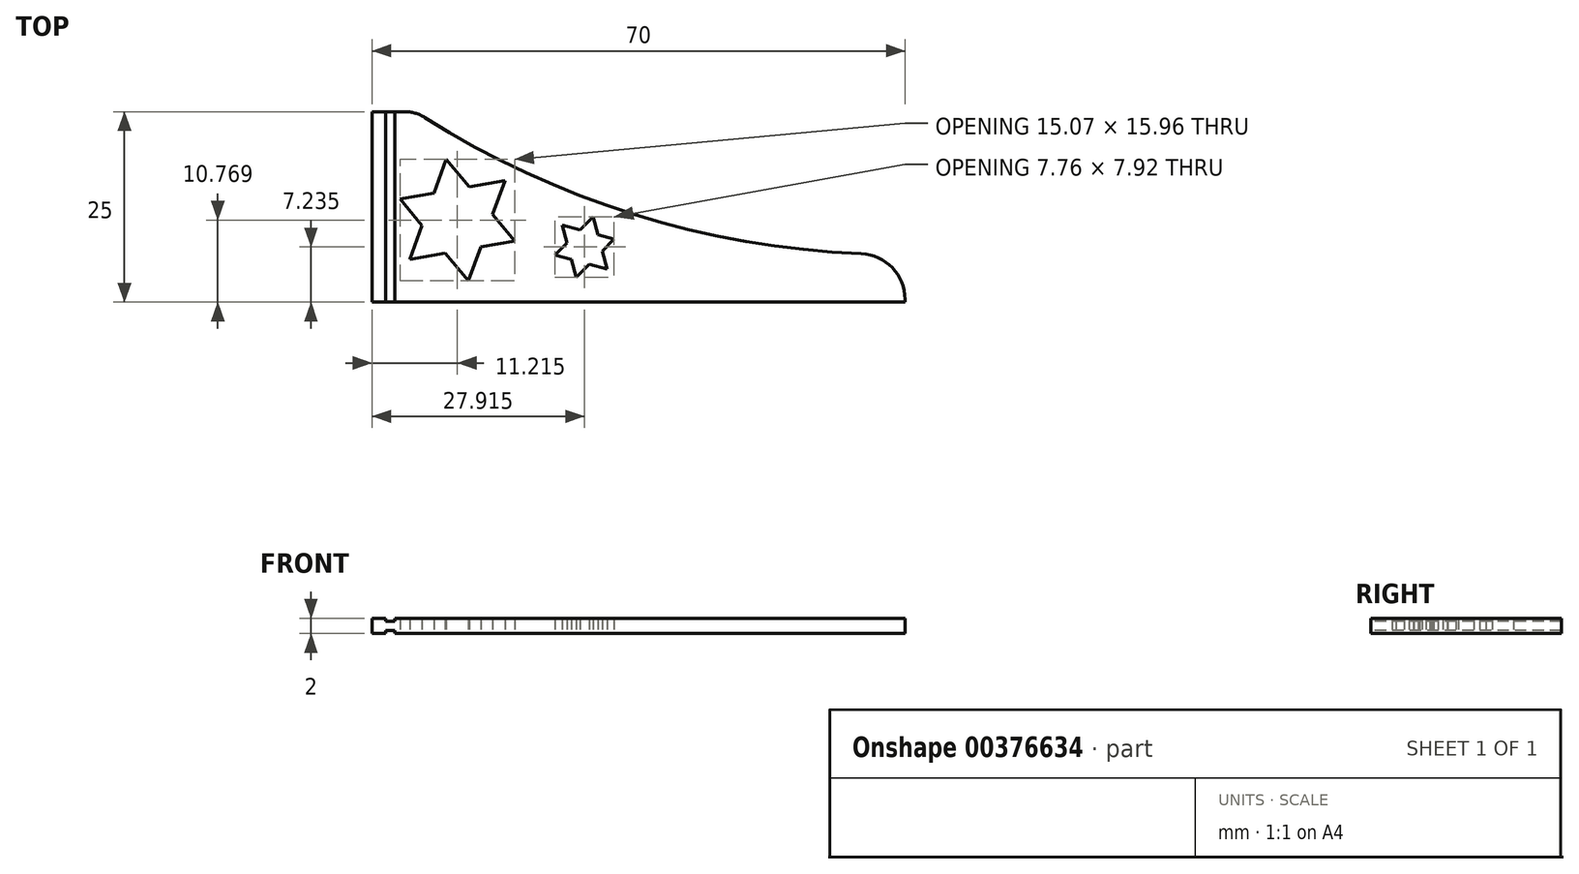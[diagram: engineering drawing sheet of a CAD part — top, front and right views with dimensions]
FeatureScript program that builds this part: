
annotation { "Feature Type Name" : "Feature", "Feature Type Description" : "" }
export const myFeature = defineFeature(function(context is Context, id is Id, definition is map)
    precondition{}
    {
        {
            var Q0;
            Q0=qCreatedBy(makeId("Top.planeOp"),FACE);
            var sketch = newSketch(context, id + "F0", { "sketchPlane" : qUnion([Q0])});
            skLineSegment(sketch, "E0.bottom", {"start": v(0, 0) * mm, "end": v(70, 0) * mm});
            skLineSegment(sketch, "E0.top", {"start": v(0, 25) * mm, "end": v(4.27, 25) * mm});
            skLineSegment(sketch, "E0.left", {"start": v(0, 0) * mm, "end": v(0, 25) * mm});
            skLineSegment(sketch, "E0.right", {"start": v(70, 0) * mm, "end": v(70, 0.35) * mm});
            skArc(sketch, "E1", {"start": v(6.95, 24.22) * mm, "mid": v(34.42, 11.5) * mm, "end": v(64.24, 6.35) * mm});
            skArc(sketch, "E2.filletArc", {"start": v(70, 0.35) * mm, "mid": v(68.33, 4.5) * mm, "end": v(64.24, 6.35) * mm});
            skArc(sketch, "E3.filletArc", {"start": v(6.95, 24.22) * mm, "mid": v(5.66, 24.8) * mm, "end": v(4.27, 25) * mm});
            skLineSegment(sketch, "E4", {"start": v(17.47, 15.94) * mm, "end": v(12.8, 15.12) * mm});
            skLineSegment(sketch, "E5", {"start": v(3.68, 13.51) * mm, "end": v(6.58, 10.05) * mm});
            skLineSegment(sketch, "E6", {"start": v(17.47, 15.94) * mm, "end": v(15.85, 11.49) * mm});
            skLineSegment(sketch, "E7", {"start": v(9.75, 18.75) * mm, "end": v(8.13, 14.3) * mm});
            skLineSegment(sketch, "E8", {"start": v(4.96, 5.6) * mm, "end": v(9.63, 6.42) * mm});
            skLineSegment(sketch, "E9", {"start": v(18.75, 8.03) * mm, "end": v(15.85, 11.49) * mm});
            skLineSegment(sketch, "E10.trimOffspring", {"start": v(8.13, 14.3) * mm, "end": v(3.68, 13.51) * mm});
            skLineSegment(sketch, "E11.trimOffspring", {"start": v(12.8, 15.12) * mm, "end": v(9.75, 18.75) * mm});
            skLineSegment(sketch, "E12.trimOffspring", {"start": v(14.3, 7.24) * mm, "end": v(12.68, 2.79) * mm});
            skLineSegment(sketch, "E13.trimOffspring", {"start": v(14.3, 7.24) * mm, "end": v(18.75, 8.03) * mm});
            skLineSegment(sketch, "E14.trimOffspring", {"start": v(9.63, 6.42) * mm, "end": v(12.68, 2.79) * mm});
            skLineSegment(sketch, "E15.trimOffspring", {"start": v(6.58, 10.05) * mm, "end": v(4.96, 5.6) * mm});
            skLineSegment(sketch, "E16.0", {"start": v(29.03, 11.2) * mm, "end": v(27.31, 9.48) * mm});
            skLineSegment(sketch, "E16.1", {"start": v(28.52, 5) * mm, "end": v(30.86, 4.36) * mm});
            skLineSegment(sketch, "E16.2", {"start": v(30.23, 6.71) * mm, "end": v(30.86, 4.36) * mm});
            skLineSegment(sketch, "E16.3", {"start": v(30.23, 6.71) * mm, "end": v(31.8, 8.28) * mm});
            skLineSegment(sketch, "E16.4", {"start": v(31.8, 8.28) * mm, "end": v(29.66, 8.85) * mm});
            skLineSegment(sketch, "E16.5", {"start": v(26.8, 3.27) * mm, "end": v(28.52, 5) * mm});
            skLineSegment(sketch, "E16.6", {"start": v(29.03, 11.2) * mm, "end": v(29.66, 8.85) * mm});
            skLineSegment(sketch, "E16.7", {"start": v(26.17, 5.62) * mm, "end": v(26.8, 3.27) * mm});
            skLineSegment(sketch, "E16.8", {"start": v(24.03, 6.2) * mm, "end": v(26.17, 5.62) * mm});
            skLineSegment(sketch, "E16.9", {"start": v(25.6, 7.76) * mm, "end": v(24.03, 6.2) * mm});
            skLineSegment(sketch, "E16.10", {"start": v(24.97, 10.1) * mm, "end": v(25.6, 7.76) * mm});
            skLineSegment(sketch, "E16.11", {"start": v(27.31, 9.48) * mm, "end": v(24.97, 10.1) * mm});
            skSolve(sketch);
        }
        {
            var Q0;
            Q0=makeQuery(id+"F0.imprint","IMPRINT",FACE,{"disambiguationData":[TD([[makeQuery(id+"F0.imprint","IMPRINT",EDGE,{"derivedFrom":sQuery(id+"F0.wireOp",EDGE,"E0.bottom")}),1.0]])]});
            extrude(context, id + "F1", {"entities" : qUnion([Q0]), "depth" : 2 * mm});
        }
        {
            var Q0;
            Q0=makeQuery(id+"F1.opExtrude","CAP_FACE",FACE,{"disambiguationData":[OSD([sQuery(id+"F0.wireOp",EDGE,"E0.bottom"),sQuery(id+"F0.wireOp",EDGE,"E0.top"),sQuery(id+"F0.wireOp",EDGE,"E0.left"),sQuery(id+"F0.wireOp",EDGE,"E0.right"),sQuery(id+"F0.wireOp",EDGE,"E1"),sQuery(id+"F0.wireOp",EDGE,"E2.filletArc"),sQuery(id+"F0.wireOp",EDGE,"E3.filletArc"),sQuery(id+"F0.wireOp",EDGE,"E4"),sQuery(id+"F0.wireOp",EDGE,"E5"),sQuery(id+"F0.wireOp",EDGE,"E6"),sQuery(id+"F0.wireOp",EDGE,"E7"),sQuery(id+"F0.wireOp",EDGE,"E8"),sQuery(id+"F0.wireOp",EDGE,"E9"),sQuery(id+"F0.wireOp",EDGE,"E10.trimOffspring"),sQuery(id+"F0.wireOp",EDGE,"E11.trimOffspring"),sQuery(id+"F0.wireOp",EDGE,"E12.trimOffspring"),sQuery(id+"F0.wireOp",EDGE,"E13.trimOffspring"),sQuery(id+"F0.wireOp",EDGE,"E14.trimOffspring"),sQuery(id+"F0.wireOp",EDGE,"E15.trimOffspring"),sQuery(id+"F0.wireOp",EDGE,"E16.0"),sQuery(id+"F0.wireOp",EDGE,"E16.1"),sQuery(id+"F0.wireOp",EDGE,"E16.2"),sQuery(id+"F0.wireOp",EDGE,"E16.3"),sQuery(id+"F0.wireOp",EDGE,"E16.4"),sQuery(id+"F0.wireOp",EDGE,"E16.5"),sQuery(id+"F0.wireOp",EDGE,"E16.6"),sQuery(id+"F0.wireOp",EDGE,"E16.7"),sQuery(id+"F0.wireOp",EDGE,"E16.8"),sQuery(id+"F0.wireOp",EDGE,"E16.9"),sQuery(id+"F0.wireOp",EDGE,"E16.10"),sQuery(id+"F0.wireOp",EDGE,"E16.11")])],"isStart":false});
            var sketch = newSketch(context, id + "F2", { "sketchPlane" : qUnion([Q0])});
            skLineSegment(sketch, "E17.bottom", {"start": v(1.8, 25) * mm, "end": v(3, 25) * mm});
            skLineSegment(sketch, "E17.top", {"start": v(1.8, 0) * mm, "end": v(3, 0) * mm});
            skLineSegment(sketch, "E17.left", {"start": v(1.8, 25) * mm, "end": v(1.8, 0) * mm});
            skLineSegment(sketch, "E17.right", {"start": v(3, 25) * mm, "end": v(3, 0) * mm});
            skSolve(sketch);
        }
        {
            var Q0;
            Q0 = qSketchRegion(id + "F2", true);
            extrude(context, id + "F3", {"entities" : qUnion([Q0]), "operationType" : NewBodyOperationType.REMOVE, "oppositeDirection" : true, "depth" : 0.4 * mm});
        }
        {
            var Q0;
            Q0=makeQuery(id+"F1.opExtrude","CAP_FACE",FACE,{"disambiguationData":[OSD([sQuery(id+"F0.wireOp",EDGE,"E0.bottom"),sQuery(id+"F0.wireOp",EDGE,"E0.top"),sQuery(id+"F0.wireOp",EDGE,"E0.left"),sQuery(id+"F0.wireOp",EDGE,"E0.right"),sQuery(id+"F0.wireOp",EDGE,"E1"),sQuery(id+"F0.wireOp",EDGE,"E2.filletArc"),sQuery(id+"F0.wireOp",EDGE,"E3.filletArc"),sQuery(id+"F0.wireOp",EDGE,"E4"),sQuery(id+"F0.wireOp",EDGE,"E5"),sQuery(id+"F0.wireOp",EDGE,"E6"),sQuery(id+"F0.wireOp",EDGE,"E7"),sQuery(id+"F0.wireOp",EDGE,"E8"),sQuery(id+"F0.wireOp",EDGE,"E9"),sQuery(id+"F0.wireOp",EDGE,"E10.trimOffspring"),sQuery(id+"F0.wireOp",EDGE,"E11.trimOffspring"),sQuery(id+"F0.wireOp",EDGE,"E12.trimOffspring"),sQuery(id+"F0.wireOp",EDGE,"E13.trimOffspring"),sQuery(id+"F0.wireOp",EDGE,"E14.trimOffspring"),sQuery(id+"F0.wireOp",EDGE,"E15.trimOffspring"),sQuery(id+"F0.wireOp",EDGE,"E16.0"),sQuery(id+"F0.wireOp",EDGE,"E16.1"),sQuery(id+"F0.wireOp",EDGE,"E16.2"),sQuery(id+"F0.wireOp",EDGE,"E16.3"),sQuery(id+"F0.wireOp",EDGE,"E16.4"),sQuery(id+"F0.wireOp",EDGE,"E16.5"),sQuery(id+"F0.wireOp",EDGE,"E16.6"),sQuery(id+"F0.wireOp",EDGE,"E16.7"),sQuery(id+"F0.wireOp",EDGE,"E16.8"),sQuery(id+"F0.wireOp",EDGE,"E16.9"),sQuery(id+"F0.wireOp",EDGE,"E16.10"),sQuery(id+"F0.wireOp",EDGE,"E16.11")])],"isStart":true});
            var sketch = newSketch(context, id + "F4", { "sketchPlane" : qUnion([Q0])});
            skLineSegment(sketch, "E18.bottom", {"start": v(1.8, -25) * mm, "end": v(3, -25) * mm});
            skLineSegment(sketch, "E18.top", {"start": v(1.8, 0) * mm, "end": v(3, 0) * mm});
            skLineSegment(sketch, "E18.left", {"start": v(1.8, -25) * mm, "end": v(1.8, 0) * mm});
            skLineSegment(sketch, "E18.right", {"start": v(3, -25) * mm, "end": v(3, 0) * mm});
            skSolve(sketch);
        }
        {
            var Q0;
            Q0 = qSketchRegion(id + "F4", true);
            extrude(context, id + "F5", {"entities" : qUnion([Q0]), "operationType" : NewBodyOperationType.REMOVE, "oppositeDirection" : true, "depth" : 0.4 * mm});
        }
    });
